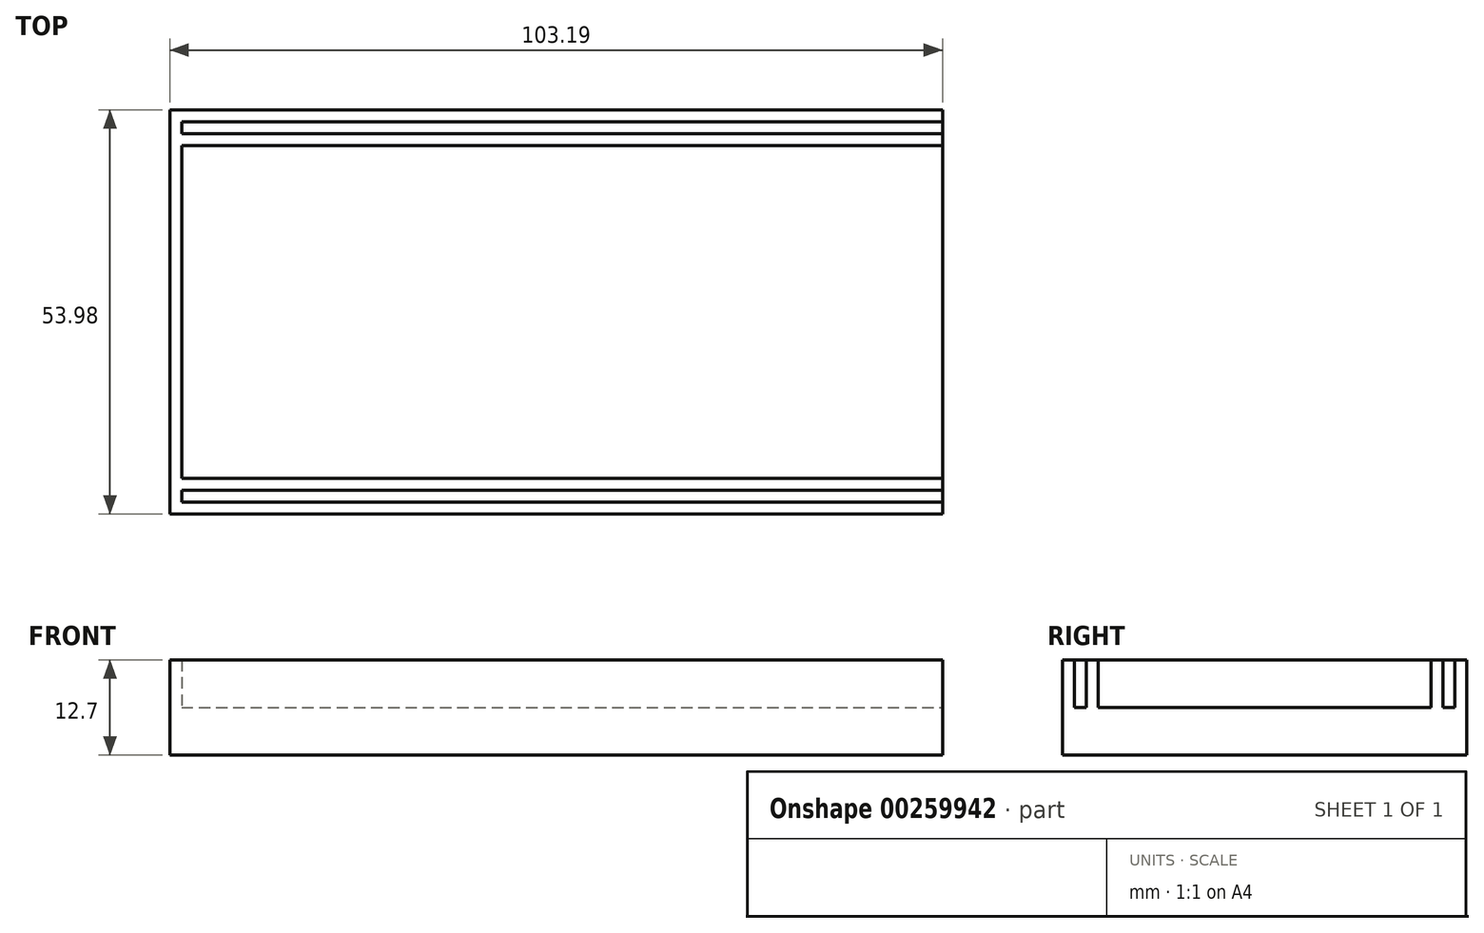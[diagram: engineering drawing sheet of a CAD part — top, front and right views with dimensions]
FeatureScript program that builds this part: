
annotation { "Feature Type Name" : "Feature", "Feature Type Description" : "" }
export const myFeature = defineFeature(function(context is Context, id is Id, definition is map)
    precondition{}
    {
        {
            var Q0;
            Q0=qCreatedBy(makeId("Top.planeOp"),FACE);
            var sketch = newSketch(context, id + "F0", { "sketchPlane" : qUnion([Q0])});
            skLineSegment(sketch, "E0.bottom", {"start": v(50.8, 25.4) * mm, "end": v(-50.8, 25.4) * mm});
            skLineSegment(sketch, "E0.top", {"start": v(50.8, -25.4) * mm, "end": v(-50.8, -25.4) * mm});
            skLineSegment(sketch, "E0.left", {"start": v(50.8, 25.4) * mm, "end": v(50.8, -25.4) * mm});
            skLineSegment(sketch, "E0.right", {"start": v(-50.8, 25.4) * mm, "end": v(-50.8, -25.4) * mm});
            skPoint(sketch, "E0.middle", {"position": v(0, 0) * mm});
            skSolve(sketch);
        }
        {
            var Q0;
            Q0 = qSketchRegion(id + "F0", true);
            extrude(context, id + "F1", {"entities" : qUnion([Q0]), "depth" : 6.35 * mm});
        }
        {
            var Q0;
            Q0=qCreatedBy(makeId("Top.planeOp"),FACE);
            var sketch = newSketch(context, id + "F2", { "sketchPlane" : qUnion([Q0])});
            skLineSegment(sketch, "E1", {"start": v(50.8, 26.99) * mm, "end": v(-52.39, 26.99) * mm});
            skLineSegment(sketch, "E2", {"start": v(-52.39, 26.99) * mm, "end": v(-52.39, -26.99) * mm});
            skLineSegment(sketch, "E3", {"start": v(-52.39, -26.99) * mm, "end": v(50.8, -26.99) * mm});
            skLineSegment(sketch, "E4", {"start": v(50.8, -26.99) * mm, "end": v(50.8, -25.4) * mm});
            skLineSegment(sketch, "E5", {"start": v(50.8, -25.4) * mm, "end": v(-50.8, -25.4) * mm});
            skLineSegment(sketch, "E6", {"start": v(-50.8, -25.4) * mm, "end": v(-50.8, -23.81) * mm});
            skLineSegment(sketch, "E7", {"start": v(-50.8, 25.4) * mm, "end": v(50.8, 25.4) * mm});
            skLineSegment(sketch, "E8", {"start": v(50.8, 26.99) * mm, "end": v(50.8, 25.4) * mm});
            skLineSegment(sketch, "E9", {"start": v(-50.8, 23.81) * mm, "end": v(50.8, 23.81) * mm});
            skLineSegment(sketch, "E10", {"start": v(50.8, 23.81) * mm, "end": v(50.8, 22.23) * mm});
            skLineSegment(sketch, "E11", {"start": v(50.8, 22.23) * mm, "end": v(-50.8, 22.23) * mm});
            skLineSegment(sketch, "E12", {"start": v(-50.8, -22.23) * mm, "end": v(50.8, -22.22) * mm});
            skLineSegment(sketch, "E13", {"start": v(50.8, -22.22) * mm, "end": v(50.8, -23.81) * mm});
            skLineSegment(sketch, "E14", {"start": v(50.8, -23.81) * mm, "end": v(-50.8, -23.81) * mm});
            skLineSegment(sketch, "E15.trimOffspring", {"start": v(-50.8, 23.81) * mm, "end": v(-50.8, 25.4) * mm});
            skLineSegment(sketch, "E16.trimOffspring", {"start": v(-50.8, -22.23) * mm, "end": v(-50.8, 22.23) * mm});
            skSolve(sketch);
        }
        {
            var Q0;
            Q0 = qSketchRegion(id + "F2", true);
            extrude(context, id + "F3", {"entities" : qUnion([Q0]), "operationType" : NewBodyOperationType.ADD, "depth" : 12.7 * mm});
        }
    });
